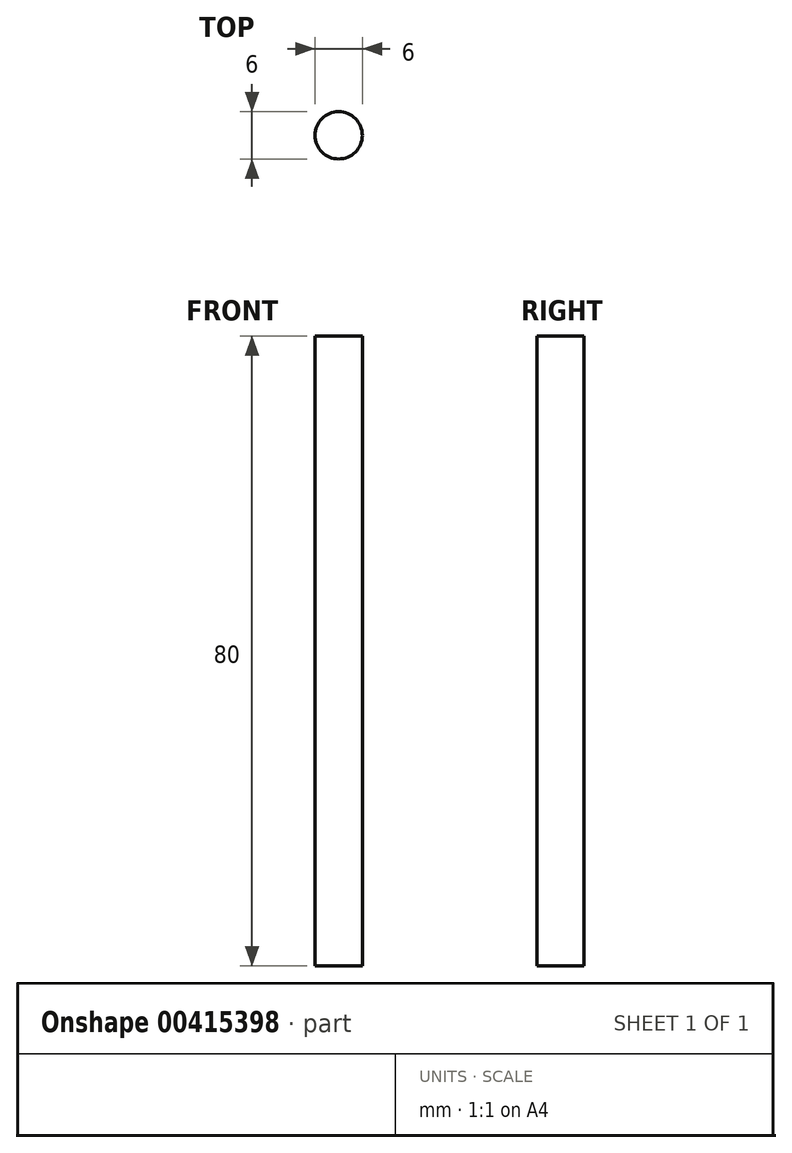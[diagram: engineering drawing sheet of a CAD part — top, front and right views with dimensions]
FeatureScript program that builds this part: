
annotation { "Feature Type Name" : "Feature", "Feature Type Description" : "" }
export const myFeature = defineFeature(function(context is Context, id is Id, definition is map)
    precondition{}
    {
        {
            var Q0;
            Q0=qCreatedBy(makeId("Top.planeOp"),FACE);
            var sketch = newSketch(context, id + "F0", { "sketchPlane" : qUnion([Q0])});
            skCircle(sketch, "E0", {"center": v(0, 0) * mm, "radius": 3 * mm});
            skSolve(sketch);
        }
        {
            var Q0;
            Q0=makeQuery(id+"F0.imprint","IMPRINT",FACE,{"disambiguationData":[TD([[makeQuery(id+"F0.imprint","IMPRINT",EDGE,{"derivedFrom":sQuery(id+"F0.wireOp",EDGE,"E0")}),1.0]])]});
            extrude(context, id + "F1", {"entities" : qUnion([Q0]), "depth" : 80 * mm, "offsetDistance" : 25 * mm});
        }
    });
